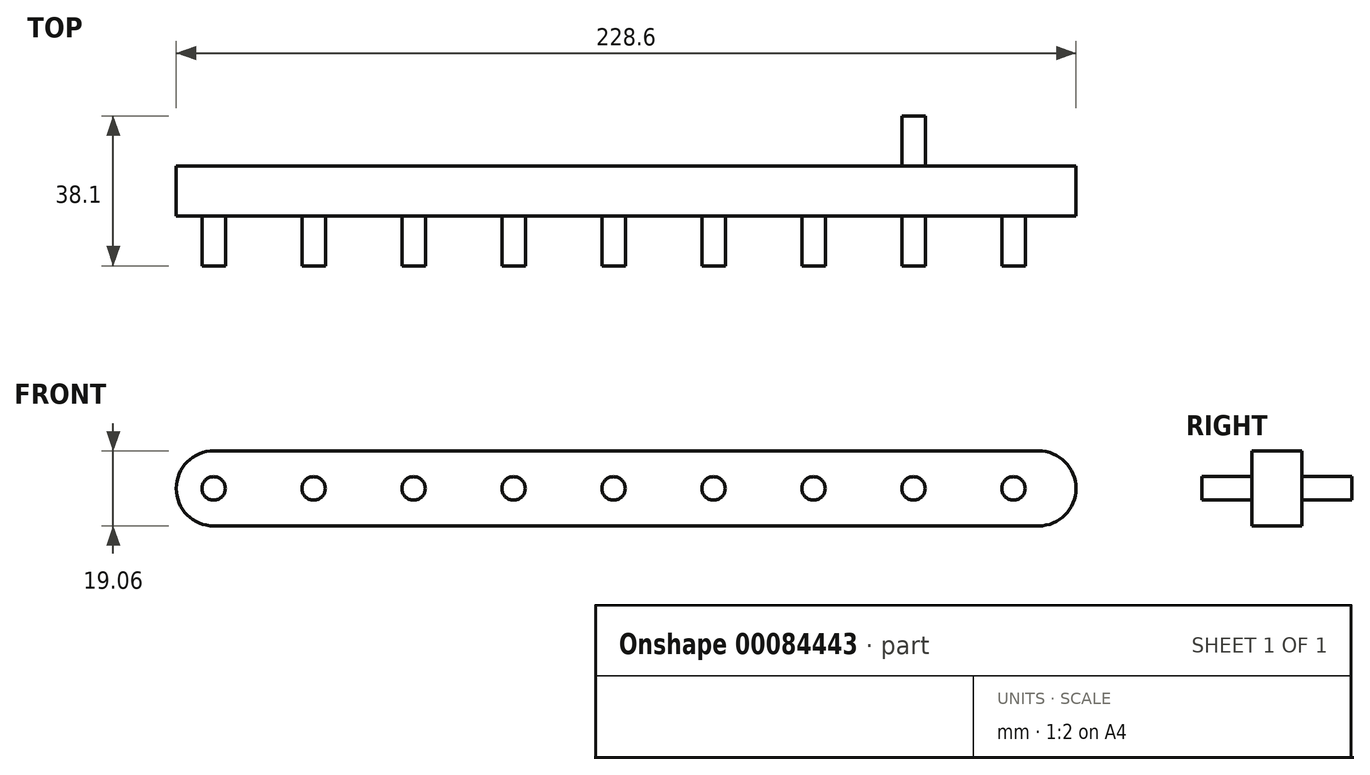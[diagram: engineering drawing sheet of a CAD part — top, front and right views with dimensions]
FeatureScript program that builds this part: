
annotation { "Feature Type Name" : "Feature", "Feature Type Description" : "" }
export const myFeature = defineFeature(function(context is Context, id is Id, definition is map)
    precondition{}
    {
        {
            var Q0;
            Q0=qCreatedBy(makeId("Front.planeOp"),FACE);
            var sketch = newSketch(context, id + "F0", { "sketchPlane" : qUnion([Q0])});
            skLineSegment(sketch, "E0.bottom", {"start": v(117.5, -9.52) * mm, "end": v(-111.1, -9.52) * mm});
            skLineSegment(sketch, "E0.top", {"start": v(117.5, 9.53) * mm, "end": v(-111.1, 9.53) * mm});
            skLineSegment(sketch, "E0.left", {"start": v(117.5, -9.52) * mm, "end": v(117.5, 9.53) * mm});
            skLineSegment(sketch, "E0.right", {"start": v(-111.1, -9.52) * mm, "end": v(-111.1, 9.53) * mm});
            skPoint(sketch, "E1.middle", {"position": v(0, 0) * mm});
            skLineSegment(sketch, "E2", {"start": v(0, 0) * mm, "end": v(0, 0) * mm});
            skCircle(sketch, "E3", {"center": v(0, 0) * mm, "radius": 2.98 * mm});
            skCircle(sketch, "E4.1.0.0", {"center": v(25.4, 0) * mm, "radius": 2.98 * mm});
            skCircle(sketch, "E4.2.0.0", {"center": v(50.8, 0) * mm, "radius": 2.98 * mm});
            skLineSegment(sketch, "E4.direction1", {"start": v(0, 0) * mm, "end": v(25.4, 0) * mm, "construction": true});
            skCircle(sketch, "E5.0.3.0", {"center": v(76.2, 0) * mm, "radius": 2.98 * mm});
            skCircle(sketch, "E5.0.4.0", {"center": v(101.6, 0) * mm, "radius": 2.98 * mm});
            skCircle(sketch, "E6.1.0.0", {"center": v(-25.4, 0) * mm, "radius": 2.98 * mm});
            skCircle(sketch, "E6.2.0.0", {"center": v(-50.8, 0) * mm, "radius": 2.98 * mm});
            skLineSegment(sketch, "E6.direction1", {"start": v(0, 0) * mm, "end": v(-25.4, 0) * mm, "construction": true});
            skCircle(sketch, "E7.0.3.0", {"center": v(-76.2, 0) * mm, "radius": 2.98 * mm});
            skCircle(sketch, "E7.0.4.0", {"center": v(-101.6, 0) * mm, "radius": 2.98 * mm});
            skSolve(sketch);
        }
        {
            var Q0;
            Q0=makeQuery(id+"F0.imprint","IMPRINT",FACE,{"disambiguationData":[TD([[makeQuery(id+"F0.imprint","IMPRINT",EDGE,{"derivedFrom":sQuery(id+"F0.wireOp",EDGE,"SHm8Pa34-JDRi-xLCb-vY8M-4y8iot5nddfY")}),1.0]])]});
            var Q1;
            Q1=makeQuery(id+"F0.imprint","IMPRINT",FACE,{"disambiguationData":[TD([[makeQuery(id+"F0.imprint","IMPRINT",EDGE,{"derivedFrom":sQuery(id+"F0.wireOp",EDGE,"E0.bottom")}),-1.0]])]});
            var Q2;
            Q2=makeQuery(id+"F0.imprint","IMPRINT",FACE,{"disambiguationData":[TD([[makeQuery(id+"F0.imprint","IMPRINT",EDGE,{"derivedFrom":sQuery(id+"F0.wireOp",EDGE,"yVfw5L5J-6KiR-xsoj-KyT5-XFOPuA5cFtkD")}),1.0]])]});
            var Q3;
            Q3=makeQuery(id+"F0.imprint","IMPRINT",FACE,{"disambiguationData":[TD([[makeQuery(id+"F0.imprint","IMPRINT",EDGE,{"derivedFrom":sQuery(id+"F0.wireOp",EDGE,"otzoMOgJ-2Fw9-6XRC-HHPs-JyfjwHity7ub")}),1.0]])]});
            extrude(context, id + "F1", {"entities" : qUnion([Q0, Q1, Q2, Q3]), "depth" : 12.7 * mm});
        }
        {
            var Q0;
            Q0=makeQuery(id+"F0.imprint","IMPRINT",FACE,{"disambiguationData":[TD([[makeQuery(id+"F0.imprint","IMPRINT",EDGE,{"derivedFrom":sQuery(id+"F0.wireOp",EDGE,"E3")}),1.0]])]});
            var Q1;
            Q1=makeQuery(id+"F0.imprint","IMPRINT",FACE,{"disambiguationData":[TD([[makeQuery(id+"F0.imprint","IMPRINT",EDGE,{"derivedFrom":sQuery(id+"F0.wireOp",EDGE,"W0BhPmkZ-Cohu-r3UB-MNsT-8zEHgvukqrbW")}),1.0]])]});
            var Q2;
            Q2=makeQuery(id+"F0.imprint","IMPRINT",FACE,{"disambiguationData":[TD([[makeQuery(id+"F0.imprint","IMPRINT",EDGE,{"derivedFrom":sQuery(id+"F0.wireOp",EDGE,"otzoMOgJ-2Fw9-6XRC-HHPs-JyfjwHity7ub")}),1.0]])]});
            var Q3;
            Q3=makeQuery(id+"F0.imprint","IMPRINT",FACE,{"disambiguationData":[TD([[makeQuery(id+"F0.imprint","IMPRINT",EDGE,{"derivedFrom":sQuery(id+"F0.wireOp",EDGE,"3Px4a1Am-neuG-O9X5-1E42-bK21xOlIPYbs")}),1.0]])]});
            var Q4;
            Q4=makeQuery(id+"F0.imprint","IMPRINT",FACE,{"disambiguationData":[TD([[makeQuery(id+"F0.imprint","IMPRINT",EDGE,{"derivedFrom":sQuery(id+"F0.wireOp",EDGE,"TvybUxnP-oc0P-UiPS-1L8a-IxXoS0crJDyP")}),1.0]])]});
            var Q5;
            Q5=makeQuery(id+"F0.imprint","IMPRINT",FACE,{"disambiguationData":[TD([[makeQuery(id+"F0.imprint","IMPRINT",EDGE,{"derivedFrom":sQuery(id+"F0.wireOp",EDGE,"yVfw5L5J-6KiR-xsoj-KyT5-XFOPuA5cFtkD")}),1.0]])]});
            var Q6;
            Q6=makeQuery(id+"F0.imprint","IMPRINT",FACE,{"disambiguationData":[TD([[makeQuery(id+"F0.imprint","IMPRINT",EDGE,{"derivedFrom":sQuery(id+"F0.wireOp",EDGE,"E7.0.4.0")}),1.0]])]});
            var Q7;
            Q7=makeQuery(id+"F0.imprint","IMPRINT",FACE,{"disambiguationData":[TD([[makeQuery(id+"F0.imprint","IMPRINT",EDGE,{"derivedFrom":sQuery(id+"F0.wireOp",EDGE,"E7.0.3.0")}),1.0]])]});
            var Q8;
            Q8=makeQuery(id+"F0.imprint","IMPRINT",FACE,{"disambiguationData":[TD([[makeQuery(id+"F0.imprint","IMPRINT",EDGE,{"derivedFrom":sQuery(id+"F0.wireOp",EDGE,"E6.2.0.0")}),1.0]])]});
            var Q9;
            Q9=makeQuery(id+"F0.imprint","IMPRINT",FACE,{"disambiguationData":[TD([[makeQuery(id+"F0.imprint","IMPRINT",EDGE,{"derivedFrom":sQuery(id+"F0.wireOp",EDGE,"E6.1.0.0")}),1.0]])]});
            var Q10;
            Q10=makeQuery(id+"F0.imprint","IMPRINT",FACE,{"disambiguationData":[TD([[makeQuery(id+"F0.imprint","IMPRINT",EDGE,{"derivedFrom":sQuery(id+"F0.wireOp",EDGE,"E4.1.0.0")}),1.0]])]});
            var Q11;
            Q11=makeQuery(id+"F0.imprint","IMPRINT",FACE,{"disambiguationData":[TD([[makeQuery(id+"F0.imprint","IMPRINT",EDGE,{"derivedFrom":sQuery(id+"F0.wireOp",EDGE,"E4.2.0.0")}),1.0]])]});
            var Q12;
            Q12=makeQuery(id+"F0.imprint","IMPRINT",FACE,{"disambiguationData":[TD([[makeQuery(id+"F0.imprint","IMPRINT",EDGE,{"derivedFrom":sQuery(id+"F0.wireOp",EDGE,"E5.0.3.0")}),1.0]])]});
            var Q13;
            Q13=makeQuery(id+"F0.imprint","IMPRINT",FACE,{"disambiguationData":[TD([[makeQuery(id+"F0.imprint","IMPRINT",EDGE,{"derivedFrom":sQuery(id+"F0.wireOp",EDGE,"E5.0.4.0")}),1.0]])]});
            extrude(context, id + "F2", {"entities" : qUnion([Q0, Q1, Q2, Q3, Q4, Q5, Q6, Q7, Q8, Q9, Q10, Q11, Q12, Q13]), "operationType" : NewBodyOperationType.ADD, "depth" : 25.4 * mm});
        }
        {
            var Q0;
            {var subQ0=sQuery(id+"F0.wireOp",EDGE,"3Px4a1Am-neuG-O9X5-1E42-bK21xOlIPYbs");var subQ1=sQuery(id+"F0.wireOp",EDGE,"E3");var subQ2=sQuery(id+"F0.wireOp",EDGE,"TvybUxnP-oc0P-UiPS-1L8a-IxXoS0crJDyP");Q0=makeQuery(id+"F2.boolean.opBoolean","MERGE",FACE,{"derivedFrom":[makeQuery(id+"F1.opExtrude","CAP_FACE",FACE,{"disambiguationData":[OSD([sQuery(id+"F0.wireOp",EDGE,"E0.bottom"),sQuery(id+"F0.wireOp",EDGE,"E0.top"),sQuery(id+"F0.wireOp",EDGE,"E0.left"),sQuery(id+"F0.wireOp",EDGE,"E0.right"),subQ2,subQ1,subQ0])],"isStart":true}),makeQuery(id+"F2.opExtrude","CAP_FACE",FACE,{"disambiguationData":[OSD([subQ2])],"isStart":true}),makeQuery(id+"F2.opExtrude","CAP_FACE",FACE,{"disambiguationData":[OSD([subQ1])],"isStart":true}),makeQuery(id+"F2.opExtrude","CAP_FACE",FACE,{"disambiguationData":[OSD([subQ0])],"isStart":true})]});}
            var sketch = newSketch(context, id + "F3", { "sketchPlane" : qUnion([Q0])});
            skLineSegment(sketch, "E8", {"start": v(0, 0) * mm, "end": v(-76.2, 0) * mm});
            skCircle(sketch, "E9", {"center": v(-76.2, 0) * mm, "radius": 2.98 * mm});
            skSolve(sketch);
        }
        {
            var Q0;
            Q0=makeQuery(id+"F3.imprint","IMPRINT",FACE,{"disambiguationData":[TD([[makeQuery(id+"F3.imprint","IMPRINT",EDGE,{"derivedFrom":makeQuery(id+"F1.opExtrude","CAP_EDGE",EDGE,{"disambiguationData":[OSD([sQuery(id+"F0.wireOp",EDGE,"E7.0.3.0")])],"isStart":true})}),-1.0]])]});
            var Q1;
            Q1=makeQuery(id+"F3.imprint","IMPRINT",FACE,{"disambiguationData":[TD([[makeQuery(id+"F3.imprint","IMPRINT",EDGE,{"derivedFrom":sQuery(id+"F3.wireOp",EDGE,"E9")}),1.0]])]});
            extrude(context, id + "F4", {"entities" : qUnion([Q0, Q1]), "operationType" : NewBodyOperationType.ADD, "depth" : 12.7 * mm});
        }
        {
            var Q0;
            Q0=makeQuery(id+"F1.opExtrude","SWEPT_EDGE",EDGE,{"disambiguationData":[OSD([sQuery(id+"F0.wireOp",EDGE,"E0.top"),sQuery(id+"F0.wireOp",EDGE,"E0.left")])]});
            var Q1;
            Q1=makeQuery(id+"F1.opExtrude","SWEPT_EDGE",EDGE,{"disambiguationData":[OSD([sQuery(id+"F0.wireOp",EDGE,"E0.bottom"),sQuery(id+"F0.wireOp",EDGE,"E0.left")])]});
            var Q2;
            Q2=makeQuery(id+"F1.opExtrude","SWEPT_EDGE",EDGE,{"disambiguationData":[OSD([sQuery(id+"F0.wireOp",EDGE,"E0.top"),sQuery(id+"F0.wireOp",EDGE,"E0.right")])]});
            var Q3;
            Q3=makeQuery(id+"F1.opExtrude","SWEPT_EDGE",EDGE,{"disambiguationData":[OSD([sQuery(id+"F0.wireOp",EDGE,"E0.bottom"),sQuery(id+"F0.wireOp",EDGE,"E0.right")])]});
            fillet(context, id + "F5", {"entities" : qUnion([Q0, Q1, Q2, Q3]), "radius" : 9.52 * mm, "tangentPropagation" : true, "allowEdgeOverflow" : false});
        }
    });
